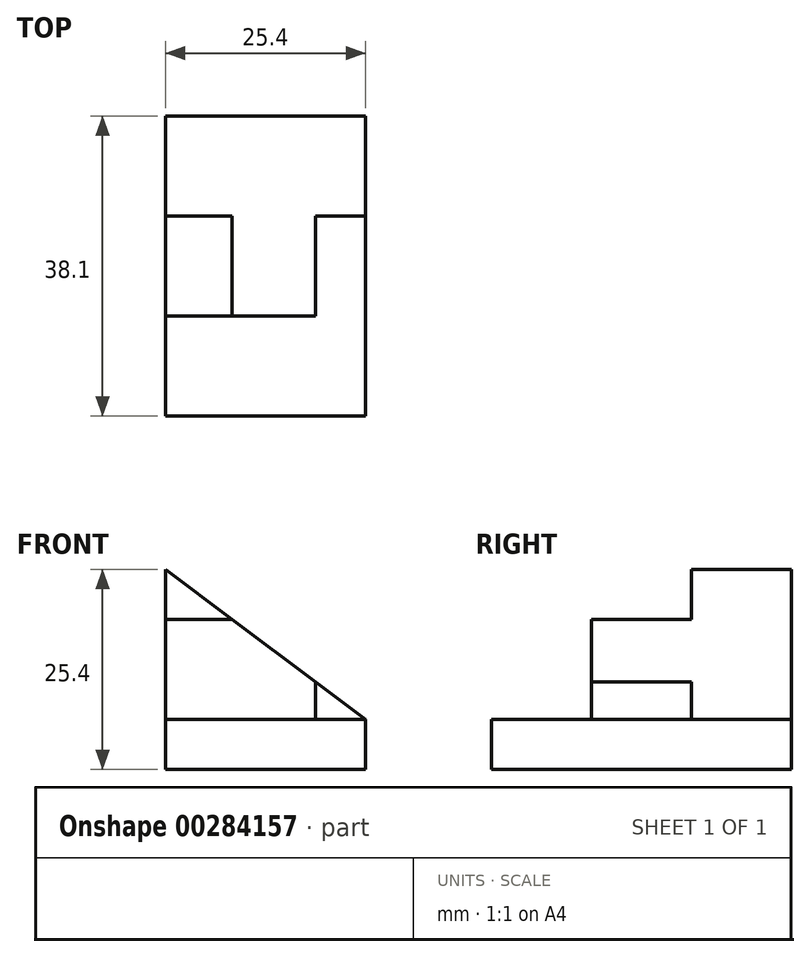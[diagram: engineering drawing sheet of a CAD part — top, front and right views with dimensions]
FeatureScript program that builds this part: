
annotation { "Feature Type Name" : "Feature", "Feature Type Description" : "" }
export const myFeature = defineFeature(function(context is Context, id is Id, definition is map)
    precondition{}
    {
        {
            var Q0;
            Q0=qCreatedBy(makeId("Front.planeOp"),FACE);
            var sketch = newSketch(context, id + "F0", { "sketchPlane" : qUnion([Q0])});
            skLineSegment(sketch, "E0", {"start": v(0, 0) * mm, "end": v(0, 25.4) * mm});
            skLineSegment(sketch, "E1", {"start": v(0, 25.4) * mm, "end": v(25.4, 6.35) * mm});
            skLineSegment(sketch, "E2", {"start": v(25.4, 6.35) * mm, "end": v(25.4, 0) * mm});
            skLineSegment(sketch, "E3", {"start": v(25.4, 0) * mm, "end": v(0, 0) * mm});
            skLineSegment(sketch, "E4", {"start": v(0, 19.05) * mm, "end": v(8.47, 19.05) * mm});
            skLineSegment(sketch, "E5", {"start": v(0, 6.35) * mm, "end": v(25.4, 6.35) * mm});
            skLineSegment(sketch, "E6", {"start": v(19.05, 6.35) * mm, "end": v(19.05, 11.11) * mm});
            skSolve(sketch);
        }
        {
            var Q0;
            {var subQ5=sQuery(id+"F0.wireOp",EDGE,"E2");Q0=makeQuery(id+"F0.imprint","IMPRINT",FACE,{"disambiguationData":[TD([[makeQuery(id+"F0.imprint","IMPRINT",EDGE,{"derivedFrom":subQ5}),-1.0]])]});}
            extrude(context, id + "F1", {"entities" : qUnion([Q0]), "depth" : 38.1 * mm});
        }
        {
            var Q0;
            {var subQ0=sQuery(id+"F0.wireOp",EDGE,"E4");Q0=makeQuery(id+"F0.imprint","IMPRINT",FACE,{"disambiguationData":[TD([[makeQuery(id+"F0.imprint","IMPRINT",EDGE,{"derivedFrom":subQ0}),-1.0]])]});}
            extrude(context, id + "F2", {"entities" : qUnion([Q0]), "operationType" : NewBodyOperationType.ADD, "depth" : 25.4 * mm});
        }
        {
            var Q0;
            {var subQ3=sQuery(id+"F0.wireOp",EDGE,"E6");Q0=makeQuery(id+"F0.imprint","IMPRINT",FACE,{"disambiguationData":[TD([[makeQuery(id+"F0.imprint","IMPRINT",EDGE,{"derivedFrom":subQ3}),-1.0]])]});}
            var Q1;
            {var subQ3=sQuery(id+"F0.wireOp",EDGE,"E4");Q1=makeQuery(id+"F0.imprint","IMPRINT",FACE,{"disambiguationData":[TD([[makeQuery(id+"F0.imprint","IMPRINT",EDGE,{"derivedFrom":subQ3}),1.0]])]});}
            extrude(context, id + "F3", {"entities" : qUnion([Q0, Q1]), "operationType" : NewBodyOperationType.ADD, "depth" : 12.7 * mm});
        }
    });
